# Revit family: Domotics-DomesticRanges-GEWISS-CHORUS_DATA-SOCKET-OUTLET_SELV
name_source: partatom
category: Apparecchi elettrici
revit_build: Autodesk Revit 2016 (Build: 20161004_0715(x64)
units: mm (PartAtom-declared; Revit-internal decimal feet)

## family parameters
Condiviso = Sì
Host = Superficie
Mantenere orientamento annotazione = Sì
Punto di calcolo locali = Sì
Quota connettore circolare = Usa diametro
Taglio con vuoti quando caricato = Sì
Tipo di parte = Normale

## types (3) — shared parameters
Carico apparente = 0 VA
Catalogue = DOMOTICS
Catalogue Range = CHORUS - DOMESTIC RANGE
IDF = be757793-dc2e-4f6a-adfb-14e6e41a9da5
IDT = bdcf3c46-c2ea-42b8-8166-e16a90c5ee31
Immagine tipo = GW14451.jpg
N. poli = 1
Produttore = GEWISS S.p.A.
Prospetto di default = 1219 mm
Technical sheet = https://www.gewiss.com
Tipo_ = SYSTEM PRESE SELV_GENERICO : GW (SELV) titanio
URL = https://www.gewiss.com
Version file RFA = 19.0
Volt = 230 V

## per-type parameters (varying)
| type | Descrizione | EAN code | Electrocod | Modello |
| GW14451 - SELV SOCKET, 2P 6A 24V 1M TITANIUM | SELV SOCKET, 2P 6A 24V 1M TITANIUM | 8011564267619 | 3720 | GW14451 |
| GW12451 - SELV SOCKET 2P 6A 24V 1M BLACK | SELV SOCKET 2P 6A 24V 1M BLACK | 8011564269644 | 3721 | GW12451 |
| GW10451 - SELV SOCKET 2P 6A 24V 1M WHITE | SELV SOCKET 2P 6A 24V 1M WHITE | 8011564262614 | 3720 | GW10451 |

## geometry (parser evidence)
native form markers: Sweep x2
no freeform markers — native parametric forms only
